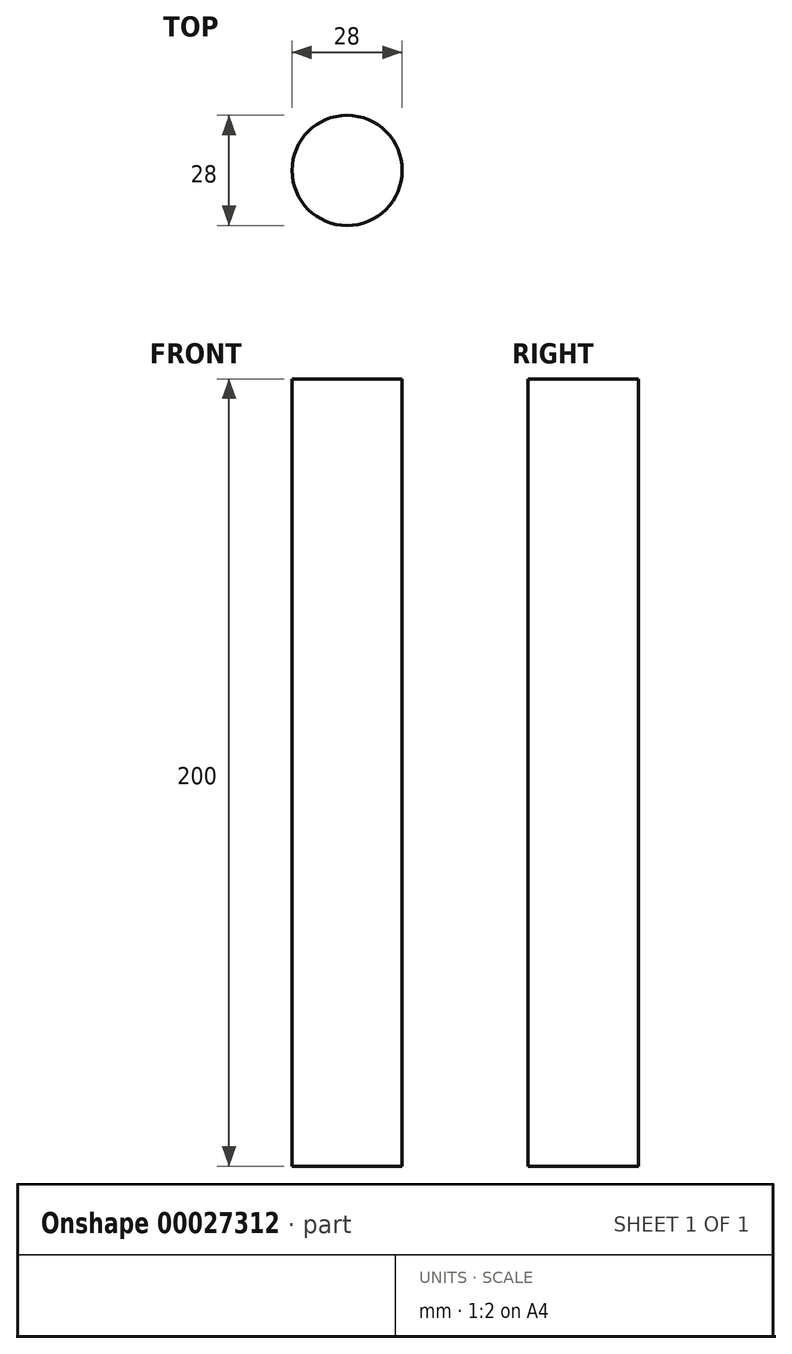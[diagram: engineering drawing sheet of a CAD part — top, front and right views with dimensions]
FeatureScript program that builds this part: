
annotation { "Feature Type Name" : "Feature", "Feature Type Description" : "" }
export const myFeature = defineFeature(function(context is Context, id is Id, definition is map)
    precondition{}
    {
        {
            var Q0;
            Q0=qCreatedBy(makeId("Top.planeOp"),FACE);
            var sketch = newSketch(context, id + "F0", { "sketchPlane" : qUnion([Q0])});
            skCircle(sketch, "E0", {"center": v(0, 0) * mm, "radius": 14 * mm});
            skSolve(sketch);
        }
        {
            var Q0;
            Q0=makeQuery(id+"F0.imprint","IMPRINT",FACE,{"disambiguationData":[TD([[makeQuery(id+"F0.imprint","IMPRINT",EDGE,{"derivedFrom":sQuery(id+"F0.wireOp",EDGE,"E0")}),1.0]])]});
            extrude(context, id + "F1", {"entities" : qUnion([Q0]), "depth" : 200 * mm});
        }
    });
